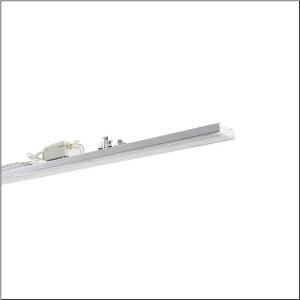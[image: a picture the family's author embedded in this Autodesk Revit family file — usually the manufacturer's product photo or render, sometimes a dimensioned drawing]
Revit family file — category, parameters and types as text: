
# Revit family: licross_r__21_recessed_mo_52tl12dv4fxg_13e3
name_source: partatom
category: Lighting Fixtures
units: mm (PartAtom-declared; Revit-internal decimal feet)

## family parameters
Cut with Voids When Loaded = No
Host = Face
Light Source = No
Part Type = Normal
Room Calculation Point = No
Round Connector Dimension = Use Diameter
Shared = No

## types (1)
- --- (1 x LED, 15420 lm, 85.3 W, 4000K)
    Apparent Load = 85 VA
    CIE Flux Codes = 72 92 99 100 100
    Color Rendering = 80
    Color Temperature = 4000K
    Default Elevation = 1800 mm
    Description = Licross® 21 Recessed MO, luminaire insert, of sheet steel, galvanised, coil coated, white, length: 2.250mm, width: 66mm, height: 67mm, LED rated luminous flux: 15.420lm, light colour: 840, control gear: DALI 2, with plug, 5-pole, with phase selection, mains connection: 220..240V, AC, 50/60Hz, rated input power: 85W, halogen-free wiring, primary optical cover: cover, of PMMA, light emission: direct distribution, primary light characteristic: symmetric, protection rating (complete): IP40, insulation class (complete): insulation class I (protective earthing), certification: CE, ENEC, VDE, UKCA, protection symbol: D if used in an environment without relevant dust loads with corresponding accessories, impact resistance: IK06, permissible ambient temperature for indoor applications: -25..+35°C, corresponds to IFS (International Featured Standards) requirements for safety and quality in the food industry, reducing of maximum allowable ambient temperature of 5°C with ceiling mounting, LABS conformity tested according to VDMA 24364:2018-05, packaging unit: 1 piece
    Height = 58 mm
    Lamp = 1 x LED
    Lamp Light Flux = 15420 lm
    Lamp Power = 85.3 W
    Lamp count = 1
    Length = 2250 mm
    Luminous efficacy = 181 lm/W
    Manufacturer = Siteco
    ModVariant = No
    Model = 52TL12DV4FXG
    Mounting Place = Ceiling
    Mounting Type = Pendant
    Number of Poles = 1
    OnlyDefault = Yes
    Power Factor = 1
    Product Name = Licross® 21 Recessed MO
    Product group = luminaire insert
    ProductGroupID = 901
    Protection Class = Protection class I
    Protection Degree = IP 40
    RLX_Detail_Level = 1
    RLX_Emergency_Light_Flux = 0 lm
    RLX_Emergency_Type = 0
    RLX_Emergency_Type_DB = No
    RlxData = <blob elided: 29633 chars, md5=f538d56f>
    Socket = socket
    Standby Power = 0 W
    System Light Flux = 15420 lm
    System Power = 85 W
    Type Comments = factory setting: luminous flux: 100 % | dim-lin: 254 | 390 mA
    Type Image = l_1296930.jpg
    URL = http://relux.com
    VarID = @adj_058031
    Voltage = 0 V
    Weight = 0.00 kg
    Width = 66 mm

## geometry (parser evidence)
native form markers: Blend x4, Sweep x12
no freeform markers — native parametric forms only
